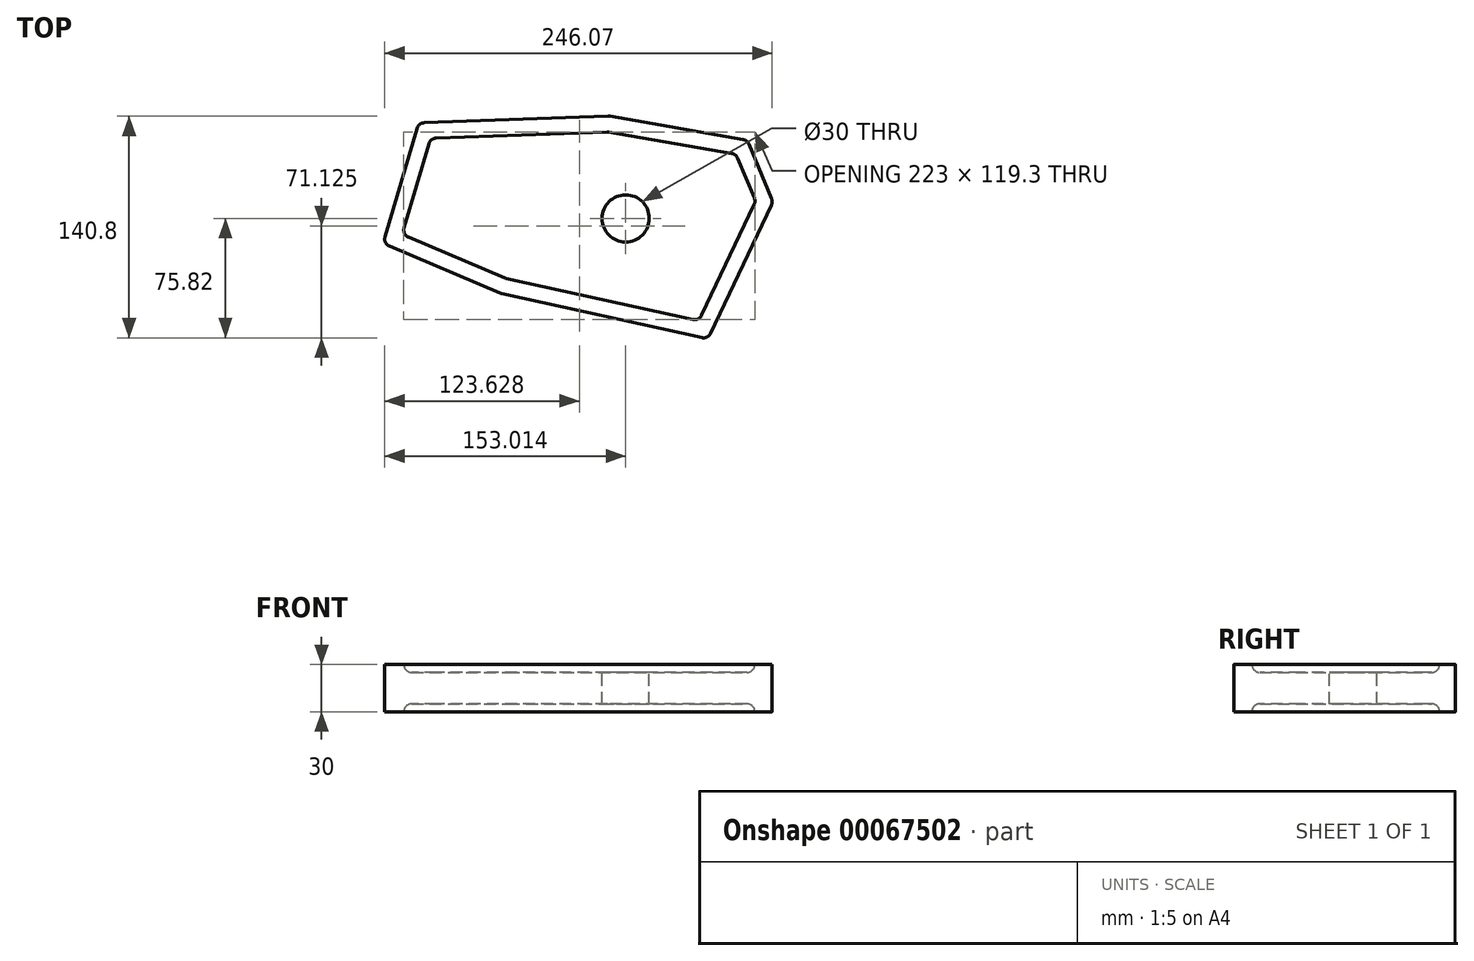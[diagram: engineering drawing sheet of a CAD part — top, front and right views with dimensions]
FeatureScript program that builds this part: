
annotation { "Feature Type Name" : "Feature", "Feature Type Description" : "" }
export const myFeature = defineFeature(function(context is Context, id is Id, definition is map)
    precondition{}
    {
        {
            var Q0;
            Q0=qCreatedBy(makeId("Top.planeOp"),FACE);
            var sketch = newSketch(context, id + "F0", { "sketchPlane" : qUnion([Q0])});
            skLineSegment(sketch, "E0", {"start": v(0, 0) * mm, "end": v(-120.94, -4.38) * mm});
            skLineSegment(sketch, "E1", {"start": v(-120.94, -4.38) * mm, "end": v(-143.52, -80.91) * mm});
            skLineSegment(sketch, "E2", {"start": v(-143.52, -80.91) * mm, "end": v(-68.74, -112.66) * mm});
            skLineSegment(sketch, "E3", {"start": v(-68.74, -112.66) * mm, "end": v(62.8, -141.56) * mm});
            skLineSegment(sketch, "E4", {"start": v(62.8, -141.56) * mm, "end": v(104.08, -54.46) * mm});
            skLineSegment(sketch, "E5", {"start": v(104.08, -54.46) * mm, "end": v(87.85, -15.31) * mm});
            skLineSegment(sketch, "E6", {"start": v(87.85, -15.31) * mm, "end": v(0, 0) * mm});
            skSolve(sketch);
        }
        {
            var Q0;
            Q0=makeQuery(id+"F0.imprint","IMPRINT",FACE,{"disambiguationData":[TD([[makeQuery(id+"F0.imprint","IMPRINT",EDGE,{"derivedFrom":sQuery(id+"F0.wireOp",EDGE,"E0")}),1.0]])]});
            extrude(context, id + "F1", {"entities" : qUnion([Q0]), "depth" : 15 * mm});
        }
        {
            var Q0;
            Q0=makeQuery(id+"F1.opExtrude","CAP_FACE",FACE,{"disambiguationData":[OSD([sQuery(id+"F0.wireOp",EDGE,"E0"),sQuery(id+"F0.wireOp",EDGE,"E1"),sQuery(id+"F0.wireOp",EDGE,"E2"),sQuery(id+"F0.wireOp",EDGE,"E3"),sQuery(id+"F0.wireOp",EDGE,"E4"),sQuery(id+"F0.wireOp",EDGE,"E5"),sQuery(id+"F0.wireOp",EDGE,"E6")])],"isStart":false});
            shell(context, id + "F2", {"entities" : qUnion([Q0]), "thickness" : 10 * mm});
        }
        {
            var Q0;
            Q0=makeQuery(id+"F1.opExtrude","SWEPT_EDGE",EDGE,{"disambiguationData":[OSD([sQuery(id+"F0.wireOp",EDGE,"E1"),sQuery(id+"F0.wireOp",EDGE,"E2")])]});
            var Q1;
            Q1=makeQuery(id+"F1.opExtrude","SWEPT_EDGE",EDGE,{"disambiguationData":[OSD([sQuery(id+"F0.wireOp",EDGE,"E2"),sQuery(id+"F0.wireOp",EDGE,"E3")])]});
            var Q2;
            Q2=makeQuery(id+"F1.opExtrude","SWEPT_EDGE",EDGE,{"disambiguationData":[OSD([sQuery(id+"F0.wireOp",EDGE,"E3"),sQuery(id+"F0.wireOp",EDGE,"E4")])]});
            var Q3;
            Q3=makeQuery(id+"F1.opExtrude","SWEPT_EDGE",EDGE,{"disambiguationData":[OSD([sQuery(id+"F0.wireOp",EDGE,"E4"),sQuery(id+"F0.wireOp",EDGE,"E5")])]});
            var Q4;
            Q4=makeQuery(id+"F1.opExtrude","SWEPT_EDGE",EDGE,{"disambiguationData":[OSD([sQuery(id+"F0.wireOp",EDGE,"E5"),sQuery(id+"F0.wireOp",EDGE,"E6")])]});
            var Q5;
            Q5=makeQuery(id+"F1.opExtrude","SWEPT_EDGE",EDGE,{"disambiguationData":[OSD([sQuery(id+"F0.wireOp",EDGE,"E0"),sQuery(id+"F0.wireOp",EDGE,"E6")])]});
            var Q6;
            Q6=makeQuery(id+"F1.opExtrude","SWEPT_EDGE",EDGE,{"disambiguationData":[OSD([sQuery(id+"F0.wireOp",EDGE,"E0"),sQuery(id+"F0.wireOp",EDGE,"E1")])]});
            var Q7;
            {var subQ0=sQuery(id+"F0.wireOp",EDGE,"E4");Q7=makeQuery(id+"F2.opShell","OFFSET_EDGE",EDGE,{"disambiguationData":[OSD([subQ0]),TDD([makeQuery(id+"F1.opExtrude","CAP_EDGE",EDGE,{"disambiguationData":[OSD([subQ0])],"isStart":true})])]});}
            var Q8;
            {var subQ0=sQuery(id+"F0.wireOp",EDGE,"E3");Q8=makeQuery(id+"F2.opShell","OFFSET_EDGE",EDGE,{"disambiguationData":[OSD([subQ0]),TDD([makeQuery(id+"F1.opExtrude","CAP_EDGE",EDGE,{"disambiguationData":[OSD([subQ0])],"isStart":true})])]});}
            var Q9;
            Q9=makeQuery(id+"F2.opShell","OFFSET_EDGE",EDGE,{"disambiguationData":[OSD([sQuery(id+"F0.wireOp",EDGE,"E3"),sQuery(id+"F0.wireOp",EDGE,"E4")])]});
            var Q10;
            Q10=makeQuery(id+"F2.opShell","OFFSET_EDGE",EDGE,{"disambiguationData":[OSD([sQuery(id+"F0.wireOp",EDGE,"E2"),sQuery(id+"F0.wireOp",EDGE,"E3")])]});
            var Q11;
            {var subQ0=sQuery(id+"F0.wireOp",EDGE,"E2");Q11=makeQuery(id+"F2.opShell","OFFSET_EDGE",EDGE,{"disambiguationData":[OSD([subQ0]),TDD([makeQuery(id+"F1.opExtrude","CAP_EDGE",EDGE,{"disambiguationData":[OSD([subQ0])],"isStart":true})])]});}
            var Q12;
            {var subQ0=sQuery(id+"F0.wireOp",EDGE,"E5");Q12=makeQuery(id+"F2.opShell","OFFSET_EDGE",EDGE,{"disambiguationData":[OSD([subQ0]),TDD([makeQuery(id+"F1.opExtrude","CAP_EDGE",EDGE,{"disambiguationData":[OSD([subQ0])],"isStart":true})])]});}
            var Q13;
            Q13=makeQuery(id+"F2.opShell","OFFSET_EDGE",EDGE,{"disambiguationData":[OSD([sQuery(id+"F0.wireOp",EDGE,"E4"),sQuery(id+"F0.wireOp",EDGE,"E5")])]});
            var Q14;
            Q14=makeQuery(id+"F2.opShell","OFFSET_EDGE",EDGE,{"disambiguationData":[OSD([sQuery(id+"F0.wireOp",EDGE,"E5"),sQuery(id+"F0.wireOp",EDGE,"E6")])]});
            var Q15;
            {var subQ0=sQuery(id+"F0.wireOp",EDGE,"E6");Q15=makeQuery(id+"F2.opShell","OFFSET_EDGE",EDGE,{"disambiguationData":[OSD([subQ0]),TDD([makeQuery(id+"F1.opExtrude","CAP_EDGE",EDGE,{"disambiguationData":[OSD([subQ0])],"isStart":true})])]});}
            var Q16;
            Q16=makeQuery(id+"F2.opShell","OFFSET_EDGE",EDGE,{"disambiguationData":[OSD([sQuery(id+"F0.wireOp",EDGE,"E0"),sQuery(id+"F0.wireOp",EDGE,"E6")])]});
            var Q17;
            {var subQ0=sQuery(id+"F0.wireOp",EDGE,"E0");Q17=makeQuery(id+"F2.opShell","OFFSET_EDGE",EDGE,{"disambiguationData":[OSD([subQ0]),TDD([makeQuery(id+"F1.opExtrude","CAP_EDGE",EDGE,{"disambiguationData":[OSD([subQ0])],"isStart":true})])]});}
            var Q18;
            {var subQ0=sQuery(id+"F0.wireOp",EDGE,"E1");Q18=makeQuery(id+"F2.opShell","OFFSET_EDGE",EDGE,{"disambiguationData":[OSD([subQ0]),TDD([makeQuery(id+"F1.opExtrude","CAP_EDGE",EDGE,{"disambiguationData":[OSD([subQ0])],"isStart":true})])]});}
            var Q19;
            Q19=makeQuery(id+"F2.opShell","OFFSET_EDGE",EDGE,{"disambiguationData":[OSD([sQuery(id+"F0.wireOp",EDGE,"E0"),sQuery(id+"F0.wireOp",EDGE,"E1")])]});
            var Q20;
            Q20=makeQuery(id+"F2.opShell","OFFSET_EDGE",EDGE,{"disambiguationData":[OSD([sQuery(id+"F0.wireOp",EDGE,"E1"),sQuery(id+"F0.wireOp",EDGE,"E2")])]});
            fillet(context, id + "F3", {"entities" : qUnion([Q0, Q1, Q2, Q3, Q4, Q5, Q6, Q7, Q8, Q9, Q10, Q11, Q12, Q13, Q14, Q15, Q16, Q17, Q18, Q19, Q20]), "radius" : 5 * mm, "tangentPropagation" : true, "allowEdgeOverflow" : false});
        }
        {
            var Q0;
            Q0=makeQuery(id+"F1.opExtrude","SWEPT_BODY",BODY,{"disambiguationData":[OSD([sQuery(id+"F0.wireOp",EDGE,"E0"),sQuery(id+"F0.wireOp",EDGE,"E1"),sQuery(id+"F0.wireOp",EDGE,"E2"),sQuery(id+"F0.wireOp",EDGE,"E3"),sQuery(id+"F0.wireOp",EDGE,"E4"),sQuery(id+"F0.wireOp",EDGE,"E5"),sQuery(id+"F0.wireOp",EDGE,"E6")])]});
            var Q1;
            Q1=qCreatedBy(makeId("Top.planeOp"),FACE);
            mirror(context, id + "F4", {"operationType" : NewBodyOperationType.ADD, "entities" : qUnion([Q0]), "mirrorPlane" : qUnion([Q1])});
        }
        {
            var Q0;
            Q0=makeQuery(id+"F2.opShell","OFFSET_FACE",FACE,{"disambiguationData":[OSD([sQuery(id+"F0.wireOp",EDGE,"E0"),sQuery(id+"F0.wireOp",EDGE,"E1"),sQuery(id+"F0.wireOp",EDGE,"E2"),sQuery(id+"F0.wireOp",EDGE,"E3"),sQuery(id+"F0.wireOp",EDGE,"E4"),sQuery(id+"F0.wireOp",EDGE,"E5"),sQuery(id+"F0.wireOp",EDGE,"E6")])]});
            var sketch = newSketch(context, id + "F5", { "sketchPlane" : qUnion([Q0])});
            skCircle(sketch, "E7", {"center": v(10.55, -65) * mm, "radius": 15 * mm});
            skSolve(sketch);
        }
        {
            var Q0;
            Q0 = qSketchRegion(id + "F5", true);
            extrude(context, id + "F6", {"entities" : qUnion([Q0]), "operationType" : NewBodyOperationType.REMOVE, "oppositeDirection" : true, "depth" : 25 * mm});
        }
    });
